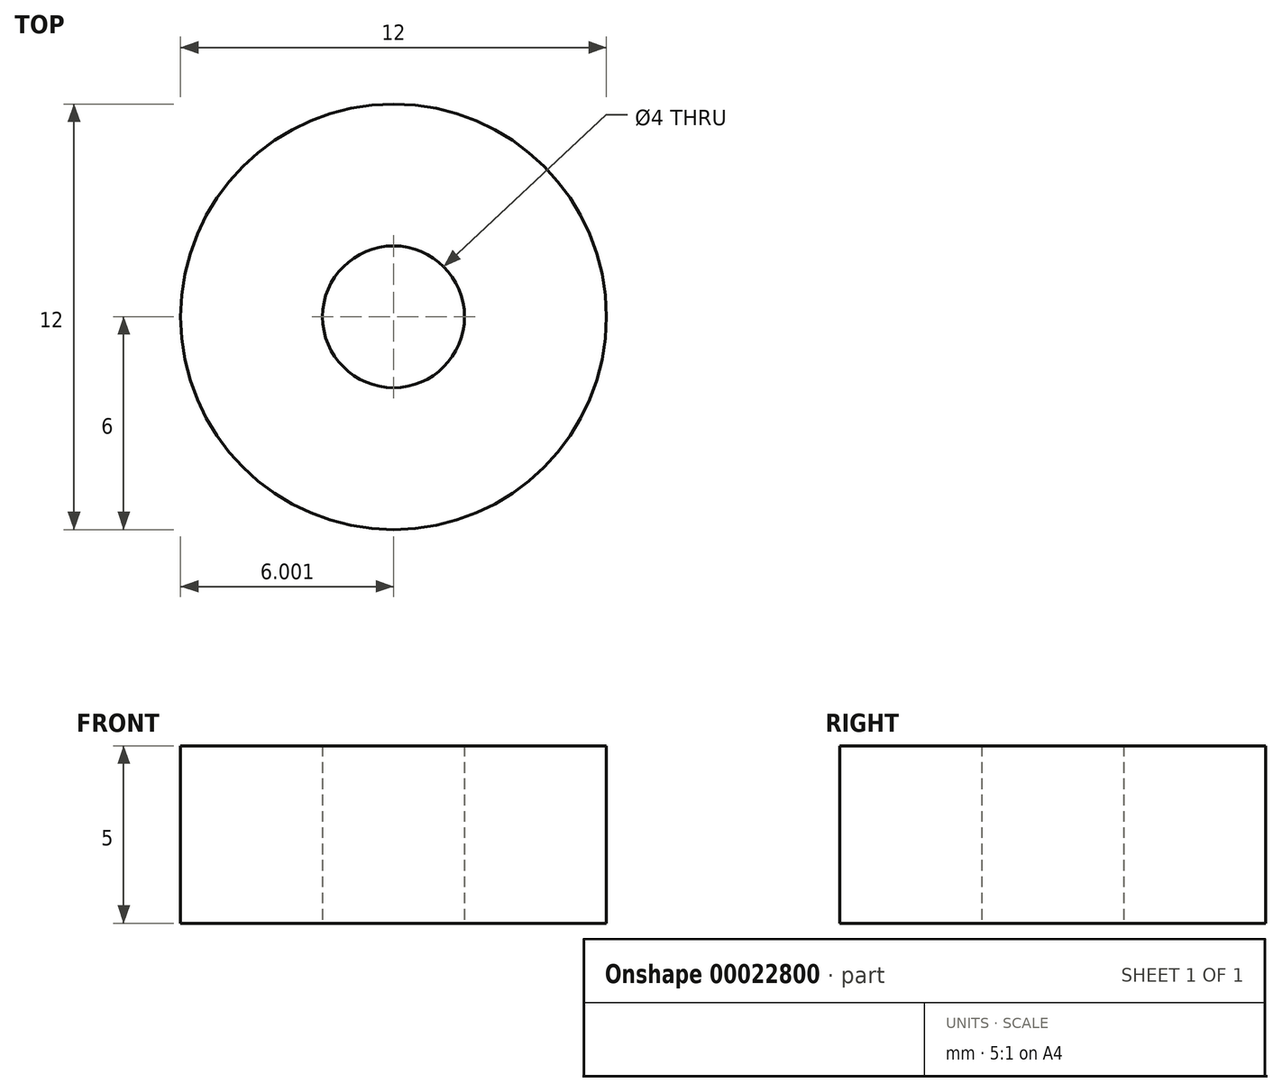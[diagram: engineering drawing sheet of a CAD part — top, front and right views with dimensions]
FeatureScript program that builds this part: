
annotation { "Feature Type Name" : "Feature", "Feature Type Description" : "" }
export const myFeature = defineFeature(function(context is Context, id is Id, definition is map)
    precondition{}
    {
        {
            var Q0;
            Q0=qCreatedBy(makeId("Top.planeOp"),FACE);
            var sketch = newSketch(context, id + "F0", { "sketchPlane" : qUnion([Q0])});
            skCircle(sketch, "E0", {"center": v(-18.76, 15.5) * mm, "radius": 6 * mm});
            skLineSegment(sketch, "E1", {"start": v(-24.45, 17.39) * mm, "end": v(-18.76, 15.5) * mm});
            skCircle(sketch, "E2", {"center": v(-18.76, 15.5) * mm, "radius": 2 * mm});
            skLineSegment(sketch, "E3", {"start": v(-18.76, 15.5) * mm, "end": v(-17.06, 16.55) * mm});
            skSolve(sketch);
        }
        {
            var Q0;
            Q0=makeQuery(id+"F0.imprint","IMPRINT",FACE,{"disambiguationData":[TD([[makeQuery(id+"F0.imprint","IMPRINT",EDGE,{"derivedFrom":sQuery(id+"F0.wireOp",EDGE,"E0")}),1.0]])]});
            extrude(context, id + "F1", {"entities" : qUnion([Q0]), "endBound" : BoundingType.SYMMETRIC, "depth" : 5 * mm});
        }
    });
